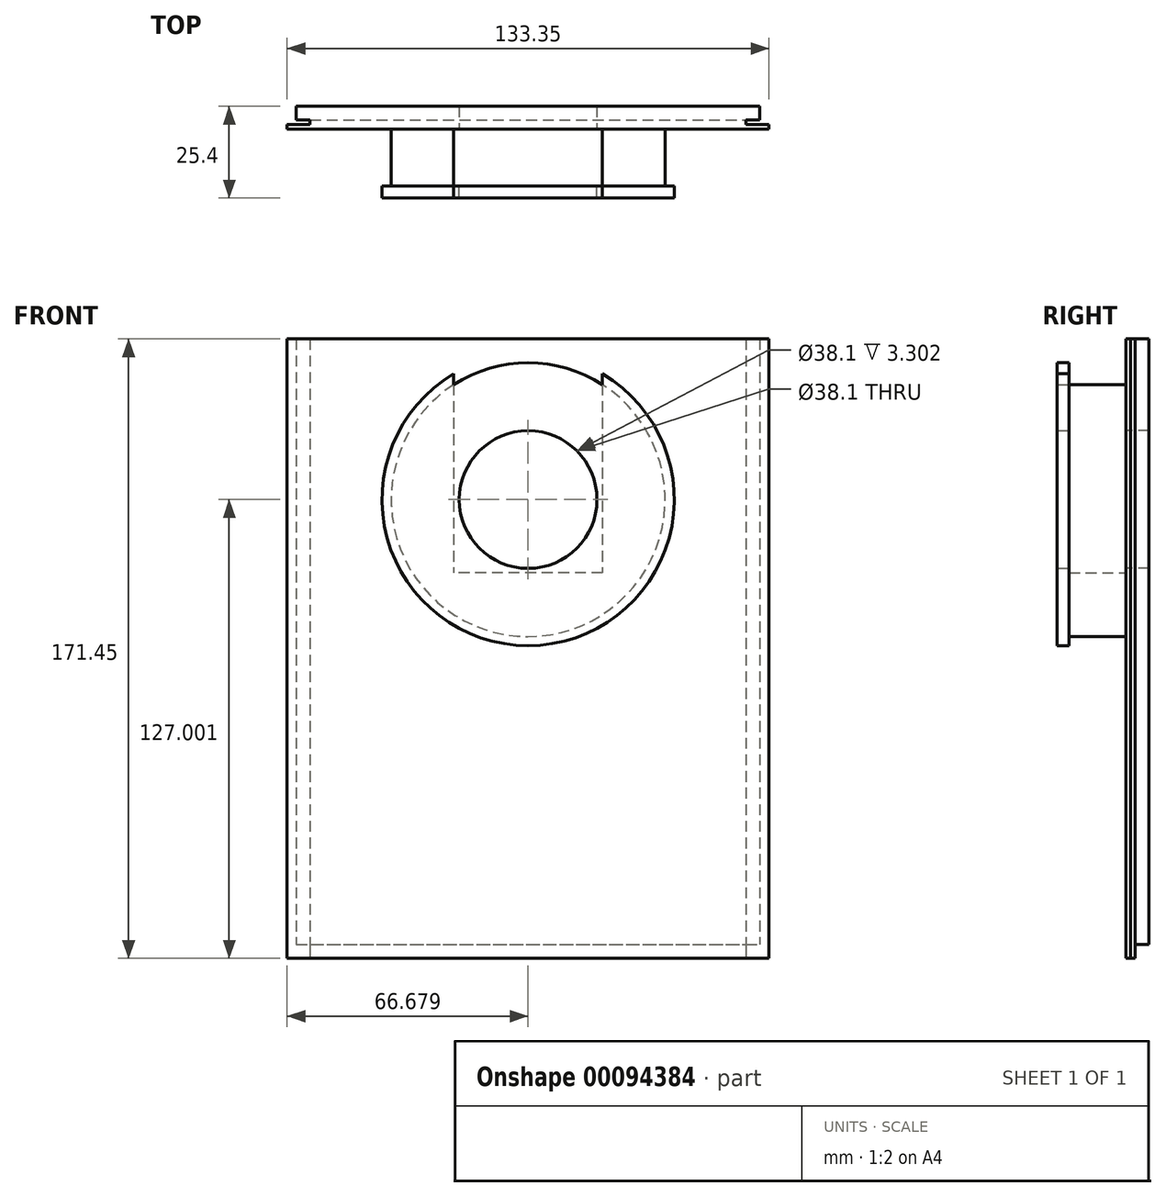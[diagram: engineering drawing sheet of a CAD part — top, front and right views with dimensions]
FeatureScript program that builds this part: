
annotation { "Feature Type Name" : "Feature", "Feature Type Description" : "" }
export const myFeature = defineFeature(function(context is Context, id is Id, definition is map)
    precondition{}
    {
        {
            var Q0;
            Q0=qCreatedBy(makeId("Front.planeOp"),FACE);
            var sketch = newSketch(context, id + "F0", { "sketchPlane" : qUnion([Q0])});
            skLineSegment(sketch, "E0.bottom", {"start": v(-99.36, -53.43) * mm, "end": v(28.91, -53.43) * mm});
            skLineSegment(sketch, "E0.top", {"start": v(-99.36, -221.07) * mm, "end": v(28.91, -221.07) * mm});
            skLineSegment(sketch, "E0.left", {"start": v(-99.36, -53.43) * mm, "end": v(-99.36, -221.07) * mm});
            skLineSegment(sketch, "E0.right", {"start": v(28.91, -53.43) * mm, "end": v(28.91, -221.07) * mm});
            skLineSegment(sketch, "E1.bottom", {"start": v(-95.55, -53.43) * mm, "end": v(25.1, -53.43) * mm});
            skLineSegment(sketch, "E1.top", {"start": v(-95.55, -224.88) * mm, "end": v(25.1, -224.88) * mm});
            skLineSegment(sketch, "E1.left", {"start": v(-95.55, -53.43) * mm, "end": v(-95.55, -224.88) * mm});
            skLineSegment(sketch, "E1.right", {"start": v(25.1, -53.43) * mm, "end": v(25.1, -224.88) * mm});
            skLineSegment(sketch, "E2.bottom", {"start": v(-101.9, -53.43) * mm, "end": v(31.45, -53.43) * mm});
            skLineSegment(sketch, "E2.top", {"start": v(-101.9, -224.88) * mm, "end": v(31.45, -224.88) * mm});
            skLineSegment(sketch, "E2.left", {"start": v(-101.9, -53.43) * mm, "end": v(-101.9, -224.88) * mm});
            skLineSegment(sketch, "E2.right", {"start": v(31.45, -53.43) * mm, "end": v(31.45, -224.88) * mm});
            skSolve(sketch);
        }
        {
            var Q0;
            {var subQ0=sQuery(id+"F0.wireOp",EDGE,"E0.left");Q0=makeQuery(id+"F0.imprint","IMPRINT",FACE,{"disambiguationData":[TD([[makeQuery(id+"F0.imprint","IMPRINT",EDGE,{"derivedFrom":subQ0}),1.0]])]});}
            var Q1;
            {var subQ0=sQuery(id+"F0.wireOp",EDGE,"E1.left");var subQ1=sQuery(id+"F0.wireOp",EDGE,"E0.top");var subQ2=makeQuery(id+"F0.imprint","INTERSECT",VERTEX,{"derivedFrom":[subQ1,subQ0]});Q1=makeQuery(id+"F0.imprint","IMPRINT",FACE,{"disambiguationData":[TD([[makeQuery(id+"F0.imprint","IMPRINT",EDGE,{"disambiguationData":[TD([[subQ2,-1.0]])],"derivedFrom":subQ1}),1.0]])]});}
            var Q2;
            {var subQ0=sQuery(id+"F0.wireOp",EDGE,"E0.right");Q2=makeQuery(id+"F0.imprint","IMPRINT",FACE,{"disambiguationData":[TD([[makeQuery(id+"F0.imprint","IMPRINT",EDGE,{"derivedFrom":subQ0}),-1.0]])]});}
            extrude(context, id + "F1", {"entities" : qUnion([Q0, Q1, Q2]), "oppositeDirection" : true, "depth" : 5.08 * mm});
        }
        {
            var Q0;
            {var subQ0=sQuery(id+"F0.wireOp",EDGE,"E1.left");var subQ1=sQuery(id+"F0.wireOp",EDGE,"E0.top");var subQ2=makeQuery(id+"F0.imprint","INTERSECT",VERTEX,{"derivedFrom":[subQ1,subQ0]});Q0=makeQuery(id+"F0.imprint","IMPRINT",FACE,{"disambiguationData":[TD([[makeQuery(id+"F0.imprint","IMPRINT",EDGE,{"disambiguationData":[TD([[subQ2,-1.0]])],"derivedFrom":subQ1}),-1.0]])]});}
            extrude(context, id + "F2", {"entities" : qUnion([Q0]), "operationType" : NewBodyOperationType.ADD, "oppositeDirection" : true, "depth" : 1.27 * mm});
        }
        {
            var Q0;
            {var subQ0=sQuery(id+"F0.wireOp",EDGE,"E0.left");Q0=makeQuery(id+"F0.imprint","IMPRINT",FACE,{"disambiguationData":[TD([[makeQuery(id+"F0.imprint","IMPRINT",EDGE,{"derivedFrom":subQ0}),1.0]])]});}
            var Q1;
            {var subQ0=sQuery(id+"F0.wireOp",EDGE,"E0.right");Q1=makeQuery(id+"F0.imprint","IMPRINT",FACE,{"disambiguationData":[TD([[makeQuery(id+"F0.imprint","IMPRINT",EDGE,{"derivedFrom":subQ0}),-1.0]])]});}
            extrude(context, id + "F3", {"entities" : qUnion([Q0, Q1]), "operationType" : NewBodyOperationType.REMOVE, "oppositeDirection" : true, "depth" : 1.27 * mm});
        }
        {
            var Q0;
            {var subQ1=sQuery(id+"F0.wireOp",EDGE,"E0.left");Q0=makeQuery(id+"F0.imprint","IMPRINT",FACE,{"disambiguationData":[TD([[makeQuery(id+"F0.imprint","IMPRINT",EDGE,{"derivedFrom":subQ1}),-1.0]])]});}
            var Q1;
            {var subQ0=sQuery(id+"F0.wireOp",EDGE,"E0.left");Q1=makeQuery(id+"F0.imprint","IMPRINT",FACE,{"disambiguationData":[TD([[makeQuery(id+"F0.imprint","IMPRINT",EDGE,{"derivedFrom":subQ0}),1.0]])]});}
            var Q2;
            {var subQ0=sQuery(id+"F0.wireOp",EDGE,"E1.left");var subQ1=sQuery(id+"F0.wireOp",EDGE,"E0.top");var subQ2=makeQuery(id+"F0.imprint","INTERSECT",VERTEX,{"derivedFrom":[subQ1,subQ0]});Q2=makeQuery(id+"F0.imprint","IMPRINT",FACE,{"disambiguationData":[TD([[makeQuery(id+"F0.imprint","IMPRINT",EDGE,{"disambiguationData":[TD([[subQ2,-1.0]])],"derivedFrom":subQ1}),1.0]])]});}
            var Q3;
            {var subQ0=sQuery(id+"F0.wireOp",EDGE,"E1.left");var subQ1=sQuery(id+"F0.wireOp",EDGE,"E0.top");var subQ2=makeQuery(id+"F0.imprint","INTERSECT",VERTEX,{"derivedFrom":[subQ1,subQ0]});Q3=makeQuery(id+"F0.imprint","IMPRINT",FACE,{"disambiguationData":[TD([[makeQuery(id+"F0.imprint","IMPRINT",EDGE,{"disambiguationData":[TD([[subQ2,-1.0]])],"derivedFrom":subQ1}),-1.0]])]});}
            var Q4;
            {var subQ0=sQuery(id+"F0.wireOp",EDGE,"E0.right");Q4=makeQuery(id+"F0.imprint","IMPRINT",FACE,{"disambiguationData":[TD([[makeQuery(id+"F0.imprint","IMPRINT",EDGE,{"derivedFrom":subQ0}),-1.0]])]});}
            var Q5;
            {var subQ1=sQuery(id+"F0.wireOp",EDGE,"E0.right");Q5=makeQuery(id+"F0.imprint","IMPRINT",FACE,{"disambiguationData":[TD([[makeQuery(id+"F0.imprint","IMPRINT",EDGE,{"derivedFrom":subQ1}),1.0]])]});}
            extrude(context, id + "F4", {"entities" : qUnion([Q0, Q1, Q2, Q3, Q4, Q5]), "operationType" : NewBodyOperationType.ADD, "depth" : 1.27 * mm});
        }
        {
            var Q0;
            Q0=makeQuery(id+"F4.opExtrude","CAP_FACE",FACE,{"disambiguationData":[OSD([sQuery(id+"F0.wireOp",EDGE,"E2.bottom"),sQuery(id+"F0.wireOp",EDGE,"E2.top"),sQuery(id+"F0.wireOp",EDGE,"E2.left"),sQuery(id+"F0.wireOp",EDGE,"E2.right")])],"isStart":false});
            var sketch = newSketch(context, id + "F5", { "sketchPlane" : qUnion([Q0])});
            skCircle(sketch, "E3", {"center": v(-35.22, -97.88) * mm, "radius": 19.05 * mm});
            skCircle(sketch, "E4", {"center": v(-35.22, -97.88) * mm, "radius": 37.9 * mm});
            skCircle(sketch, "E5", {"center": v(-35.22, -97.88) * mm, "radius": 40.44 * mm});
            skLineSegment(sketch, "E6.bottom", {"start": v(-14.65, -77.56) * mm, "end": v(-55.8, -77.56) * mm});
            skLineSegment(sketch, "E6.top", {"start": v(-14.65, -118.2) * mm, "end": v(-55.8, -118.2) * mm});
            skLineSegment(sketch, "E6.left", {"start": v(-14.65, -77.56) * mm, "end": v(-14.65, -118.2) * mm});
            skLineSegment(sketch, "E6.right", {"start": v(-55.8, -77.56) * mm, "end": v(-55.8, -118.2) * mm});
            skLineSegment(sketch, "E7.bottom", {"start": v(-8.3, -71.2) * mm, "end": v(-62.15, -71.2) * mm});
            skLineSegment(sketch, "E7.top", {"start": v(-8.3, -124.55) * mm, "end": v(-62.15, -124.55) * mm});
            skLineSegment(sketch, "E7.left", {"start": v(-8.3, -71.2) * mm, "end": v(-8.3, -124.55) * mm});
            skLineSegment(sketch, "E7.right", {"start": v(-62.15, -71.2) * mm, "end": v(-62.15, -124.55) * mm});
            skLineSegment(sketch, "E8", {"start": v(-55.8, -77.56) * mm, "end": v(-55.8, -63.07) * mm});
            skLineSegment(sketch, "E9", {"start": v(-14.65, -77.56) * mm, "end": v(-14.65, -63.07) * mm});
            skSolve(sketch);
        }
        {
            var Q0;
            {var subQ0=sQuery(id+"F5.wireOp",EDGE,"E9");var subQ1=sQuery(id+"F5.wireOp",EDGE,"E4");var subQ2=makeQuery(id+"F5.imprint","INTERSECT",VERTEX,{"derivedFrom":[subQ1,subQ0]});Q0=makeQuery(id+"F5.imprint","IMPRINT",FACE,{"disambiguationData":[TD([[makeQuery(id+"F5.imprint","IMPRINT",EDGE,{"disambiguationData":[TD([[subQ2,-1.0]])],"derivedFrom":subQ1}),1.0]])]});}
            var Q1;
            {var subQ0=sQuery(id+"F5.wireOp",EDGE,"E6.bottom");Q1=makeQuery(id+"F5.imprint","IMPRINT",FACE,{"disambiguationData":[TD([[makeQuery(id+"F5.imprint","IMPRINT",EDGE,{"derivedFrom":subQ0}),-1.0]])]});}
            var Q2;
            Q2=makeQuery(id+"F5.imprint","IMPRINT",FACE,{"disambiguationData":[TD([[makeQuery(id+"F5.imprint","IMPRINT",EDGE,{"derivedFrom":sQuery(id+"F5.wireOp",EDGE,"E3")}),-1.0]])]});
            var Q3;
            {var subQ1=sQuery(id+"F5.wireOp",EDGE,"E4");var subQ3=sQuery(id+"F5.wireOp",EDGE,"E8");var subQ4=makeQuery(id+"F5.imprint","INTERSECT",VERTEX,{"derivedFrom":[subQ1,subQ3]});Q3=makeQuery(id+"F5.imprint","IMPRINT",FACE,{"disambiguationData":[TD([[makeQuery(id+"F5.imprint","IMPRINT",EDGE,{"disambiguationData":[TD([[subQ4,1.0]])],"derivedFrom":subQ3}),1.0]])]});}
            var Q4;
            {var subQ0=sQuery(id+"F5.wireOp",EDGE,"E7.right");Q4=makeQuery(id+"F5.imprint","IMPRINT",FACE,{"disambiguationData":[TD([[makeQuery(id+"F5.imprint","IMPRINT",EDGE,{"derivedFrom":subQ0}),-1.0]])]});}
            var Q5;
            {var subQ1=sQuery(id+"F5.wireOp",EDGE,"E4");var subQ3=sQuery(id+"F5.wireOp",EDGE,"E9");var subQ4=makeQuery(id+"F5.imprint","INTERSECT",VERTEX,{"derivedFrom":[subQ1,subQ3]});Q5=makeQuery(id+"F5.imprint","IMPRINT",FACE,{"disambiguationData":[TD([[makeQuery(id+"F5.imprint","IMPRINT",EDGE,{"disambiguationData":[TD([[subQ4,1.0]])],"derivedFrom":subQ3}),-1.0]])]});}
            var Q6;
            Q6=makeQuery(id+"F5.imprint","IMPRINT",FACE,{"disambiguationData":[TD([[makeQuery(id+"F5.imprint","IMPRINT",EDGE,{"derivedFrom":sQuery(id+"F5.wireOp",EDGE,"E6.top")}),1.0]])]});
            var Q7;
            {var subQ0=sQuery(id+"F5.wireOp",EDGE,"E7.left");Q7=makeQuery(id+"F5.imprint","IMPRINT",FACE,{"disambiguationData":[TD([[makeQuery(id+"F5.imprint","IMPRINT",EDGE,{"derivedFrom":subQ0}),1.0]])]});}
            var Q8;
            {var subQ0=sQuery(id+"F5.wireOp",EDGE,"E7.top");Q8=makeQuery(id+"F5.imprint","IMPRINT",FACE,{"disambiguationData":[TD([[makeQuery(id+"F5.imprint","IMPRINT",EDGE,{"derivedFrom":subQ0}),1.0]])]});}
            var Q9;
            {var subQ8=sQuery(id+"F5.wireOp",EDGE,"E8");var subQ11=sQuery(id+"F5.wireOp",EDGE,"E5");var subQ15=makeQuery(id+"F5.imprint","INTERSECT",VERTEX,{"derivedFrom":[subQ11,subQ8]});Q9=makeQuery(id+"F5.imprint","IMPRINT",FACE,{"disambiguationData":[TD([[makeQuery(id+"F5.imprint","IMPRINT",EDGE,{"disambiguationData":[TD([[subQ15,-1.0]])],"derivedFrom":subQ11}),1.0]])]});}
            extrude(context, id + "F6", {"entities" : qUnion([Q0, Q1, Q2, Q3, Q4, Q5, Q6, Q7, Q8, Q9]), "operationType" : NewBodyOperationType.ADD, "depth" : 19.05 * mm});
        }
        {
            var Q0;
            Q0=makeQuery(id+"F5.imprint","IMPRINT",FACE,{"disambiguationData":[TD([[makeQuery(id+"F5.imprint","IMPRINT",EDGE,{"derivedFrom":sQuery(id+"F5.wireOp",EDGE,"E3")}),-1.0]])]});
            var Q1;
            {var subQ0=sQuery(id+"F5.wireOp",EDGE,"E6.bottom");Q1=makeQuery(id+"F5.imprint","IMPRINT",FACE,{"disambiguationData":[TD([[makeQuery(id+"F5.imprint","IMPRINT",EDGE,{"derivedFrom":subQ0}),-1.0]])]});}
            var Q2;
            {var subQ0=sQuery(id+"F5.wireOp",EDGE,"E9");var subQ1=sQuery(id+"F5.wireOp",EDGE,"E4");var subQ2=makeQuery(id+"F5.imprint","INTERSECT",VERTEX,{"derivedFrom":[subQ1,subQ0]});Q2=makeQuery(id+"F5.imprint","IMPRINT",FACE,{"disambiguationData":[TD([[makeQuery(id+"F5.imprint","IMPRINT",EDGE,{"disambiguationData":[TD([[subQ2,-1.0]])],"derivedFrom":subQ1}),1.0]])]});}
            var Q3;
            {var subQ0=sQuery(id+"F5.wireOp",EDGE,"E9");var subQ1=sQuery(id+"F5.wireOp",EDGE,"E4");var subQ2=makeQuery(id+"F5.imprint","INTERSECT",VERTEX,{"derivedFrom":[subQ1,subQ0]});Q3=makeQuery(id+"F5.imprint","IMPRINT",FACE,{"disambiguationData":[TD([[makeQuery(id+"F5.imprint","IMPRINT",EDGE,{"disambiguationData":[TD([[subQ2,-1.0]])],"derivedFrom":subQ1}),-1.0]])]});}
            var Q4;
            {var subQ8=sQuery(id+"F5.wireOp",EDGE,"E8");var subQ11=sQuery(id+"F5.wireOp",EDGE,"E5");var subQ15=makeQuery(id+"F5.imprint","INTERSECT",VERTEX,{"derivedFrom":[subQ11,subQ8]});Q4=makeQuery(id+"F5.imprint","IMPRINT",FACE,{"disambiguationData":[TD([[makeQuery(id+"F5.imprint","IMPRINT",EDGE,{"disambiguationData":[TD([[subQ15,-1.0]])],"derivedFrom":subQ11}),1.0]])]});}
            extrude(context, id + "F7", {"entities" : qUnion([Q0, Q1, Q2, Q3, Q4]), "operationType" : NewBodyOperationType.REMOVE, "depth" : 15.75 * mm});
        }
        {
            var Q0;
            Q0=makeQuery(id+"F5.imprint","IMPRINT",FACE,{"disambiguationData":[TD([[makeQuery(id+"F5.imprint","IMPRINT",EDGE,{"derivedFrom":sQuery(id+"F5.wireOp",EDGE,"E3")}),1.0]])]});
            extrude(context, id + "F8", {"entities" : qUnion([Q0]), "operationType" : NewBodyOperationType.REMOVE, "oppositeDirection" : true, "depth" : 6.35 * mm});
        }
    });
